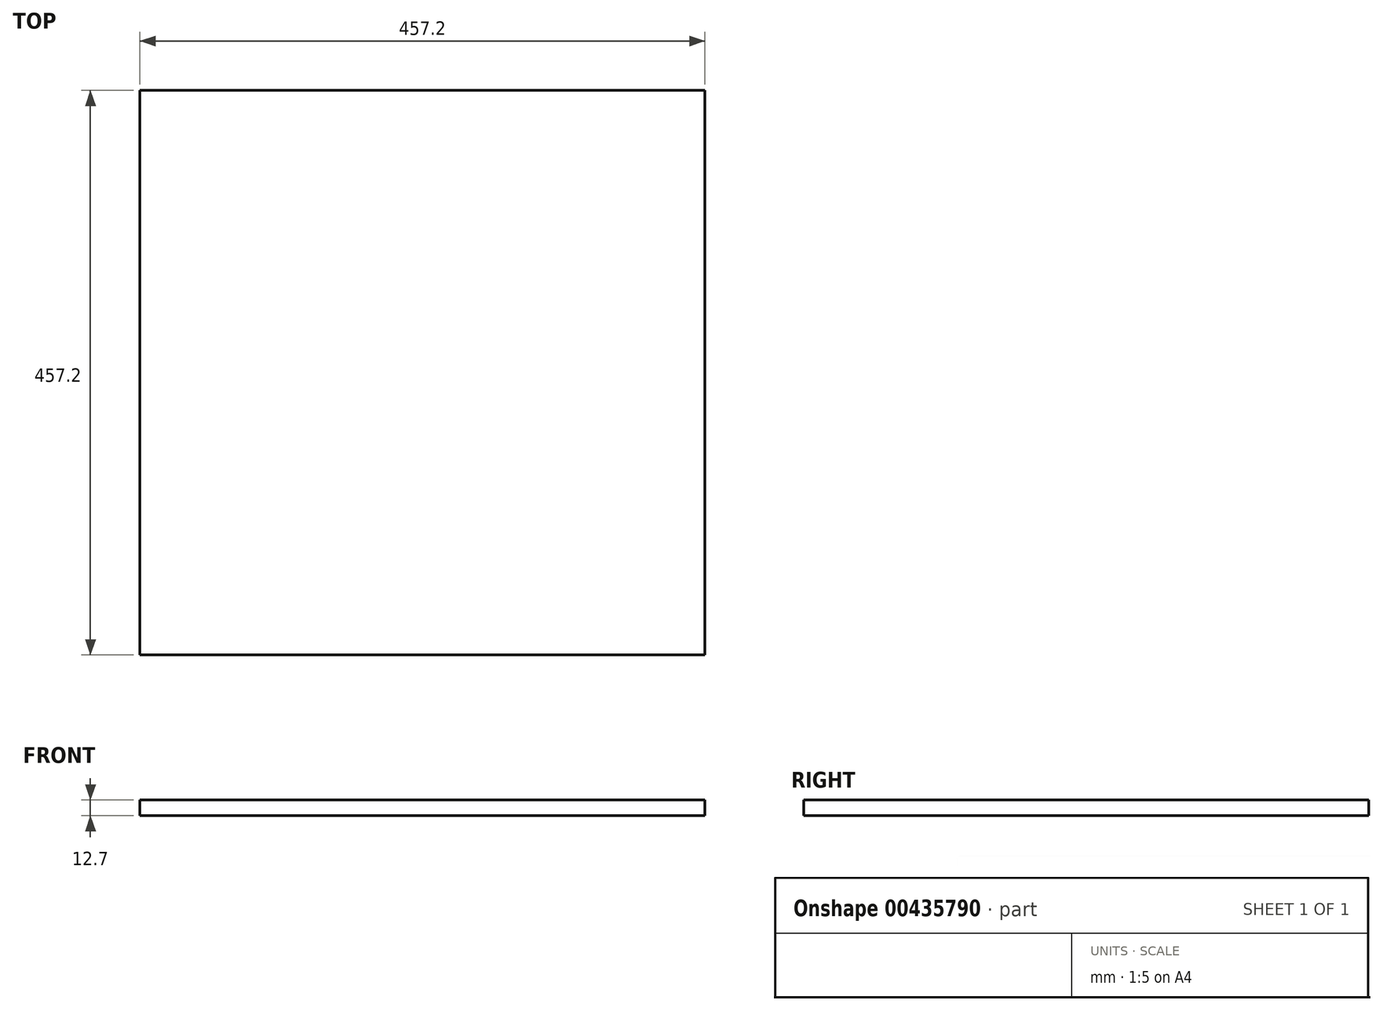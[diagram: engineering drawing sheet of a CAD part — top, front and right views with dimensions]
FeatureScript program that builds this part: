
annotation { "Feature Type Name" : "Feature", "Feature Type Description" : "" }
export const myFeature = defineFeature(function(context is Context, id is Id, definition is map)
    precondition{}
    {
        {
            var Q0;
            Q0=qCreatedBy(makeId("Top.planeOp"),FACE);
            var sketch = newSketch(context, id + "F0", { "sketchPlane" : qUnion([Q0])});
            skLineSegment(sketch, "E0.bottom", {"start": v(-228.6, 228.6) * mm, "end": v(228.6, 228.6) * mm});
            skLineSegment(sketch, "E0.top", {"start": v(-228.6, -228.6) * mm, "end": v(228.6, -228.6) * mm});
            skLineSegment(sketch, "E0.left", {"start": v(-228.6, 228.6) * mm, "end": v(-228.6, -228.6) * mm});
            skLineSegment(sketch, "E0.right", {"start": v(228.6, 228.6) * mm, "end": v(228.6, -228.6) * mm});
            skPoint(sketch, "E0.middle", {"position": v(0, 0) * mm});
            skSolve(sketch);
        }
        {
            var Q0;
            Q0=makeQuery(id+"F0.imprint","IMPRINT",FACE,{"disambiguationData":[TD([[makeQuery(id+"F0.imprint","IMPRINT",EDGE,{"derivedFrom":sQuery(id+"F0.wireOp",EDGE,"E0.bottom")}),-1.0]])]});
            extrude(context, id + "F1", {"entities" : qUnion([Q0]), "depth" : 12.7 * mm});
        }
    });
